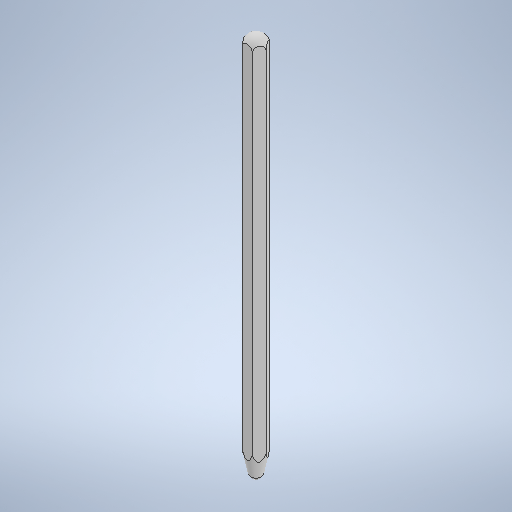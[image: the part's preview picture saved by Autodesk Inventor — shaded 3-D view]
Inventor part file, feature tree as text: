
AUTODESK INVENTOR PART (.ipt)
format: ipt  version: 2025.1 (Build 291241000, 241)  size: 305,664 bytes
history: native  units: mm
features: thicken_offset x6, sketch x5, revolve x3, extrude x2
ambient origin geometry x8: Origin, YZ Plane, XZ Plane, XY Plane, X Axis, Y Axis, Z Axis, Center Point
bodies: Solid1 (feature_tree)
feature tree (16):
  extrude  "Extrusion1"  Depth=155.0mm TaperAngle=0.0deg
  revolve  "Revolution1"  [1 undecoded]
  extrude  "Extrusion2"  Depth=10.0mm
  revolve  "Revolution2"  [1 undecoded]
  thicken_offset  "Thicken1"
  thicken_offset  "Thicken2"
  thicken_offset  "Thicken3"
  thicken_offset  "Thicken4"
  thicken_offset  "Thicken5"
  thicken_offset  "Thicken6"
  revolve  "Revolution3"  [1 undecoded]
  sketch  "Sketch1"  dims[d1=9.0mm d2=155.0mm d3=0.0mm]
  sketch  "Sketch2"  dims[d4=90.0deg d5=400.0mm d6=0.0mm]
  sketch  "Sketch3"  dims[d7=10.0mm d9=2.5mm]
  sketch  "Sketch4"  dims[d10=90.0deg d11=5.0mm]
  sketch  "Sketch5"  dims[d12=5.0mm d13=5.0mm d14=5.0mm d15=5.0mm d16=5.0mm d17=5.0mm d18=5.0mm d19=5.0mm d20=5.0mm d21=5.0mm d22=5.0mm d23=4.0mm d24=90.0deg]
note: 3 required parameter values undecoded (feature->parameter linkage not recoverable at this tier; creation-order binding heuristic only, values carry confidence <= 0.55)
